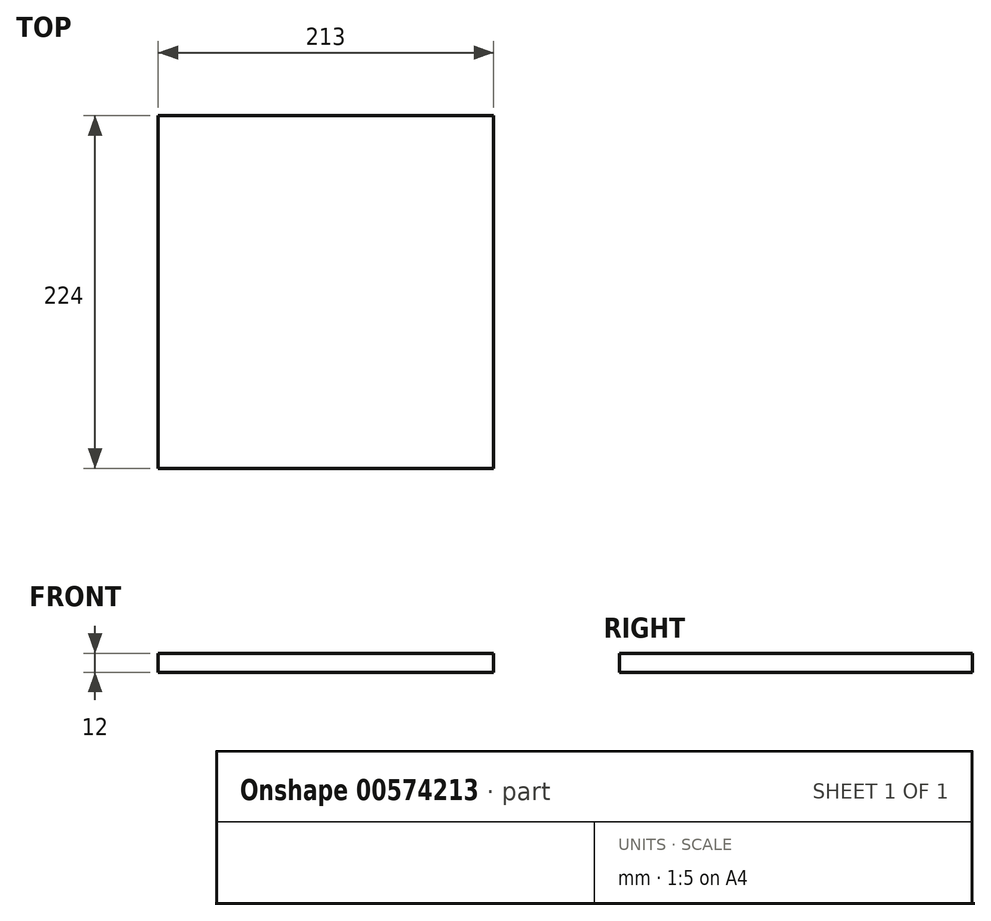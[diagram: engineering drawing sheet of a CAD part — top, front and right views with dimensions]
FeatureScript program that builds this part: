
annotation { "Feature Type Name" : "Feature", "Feature Type Description" : "" }
export const myFeature = defineFeature(function(context is Context, id is Id, definition is map)
    precondition{}
    {
        {
            var Q0;
            Q0=qCreatedBy(makeId("Top.planeOp"),FACE);
            var sketch = newSketch(context, id + "F0", { "sketchPlane" : qUnion([Q0])});
            skLineSegment(sketch, "E0.bottom", {"start": v(0, 0) * mm, "end": v(213, 0) * mm});
            skLineSegment(sketch, "E0.top", {"start": v(0, 224) * mm, "end": v(213, 224) * mm});
            skLineSegment(sketch, "E0.left", {"start": v(0, 0) * mm, "end": v(0, 224) * mm});
            skLineSegment(sketch, "E0.right", {"start": v(213, 0) * mm, "end": v(213, 224) * mm});
            skSolve(sketch);
        }
        {
            var Q0;
            Q0 = qSketchRegion(id + "F0", true);
            extrude(context, id + "F1", {"entities" : qUnion([Q0]), "depth" : 12 * mm, "offsetDistance" : 25 * mm});
        }
    });
